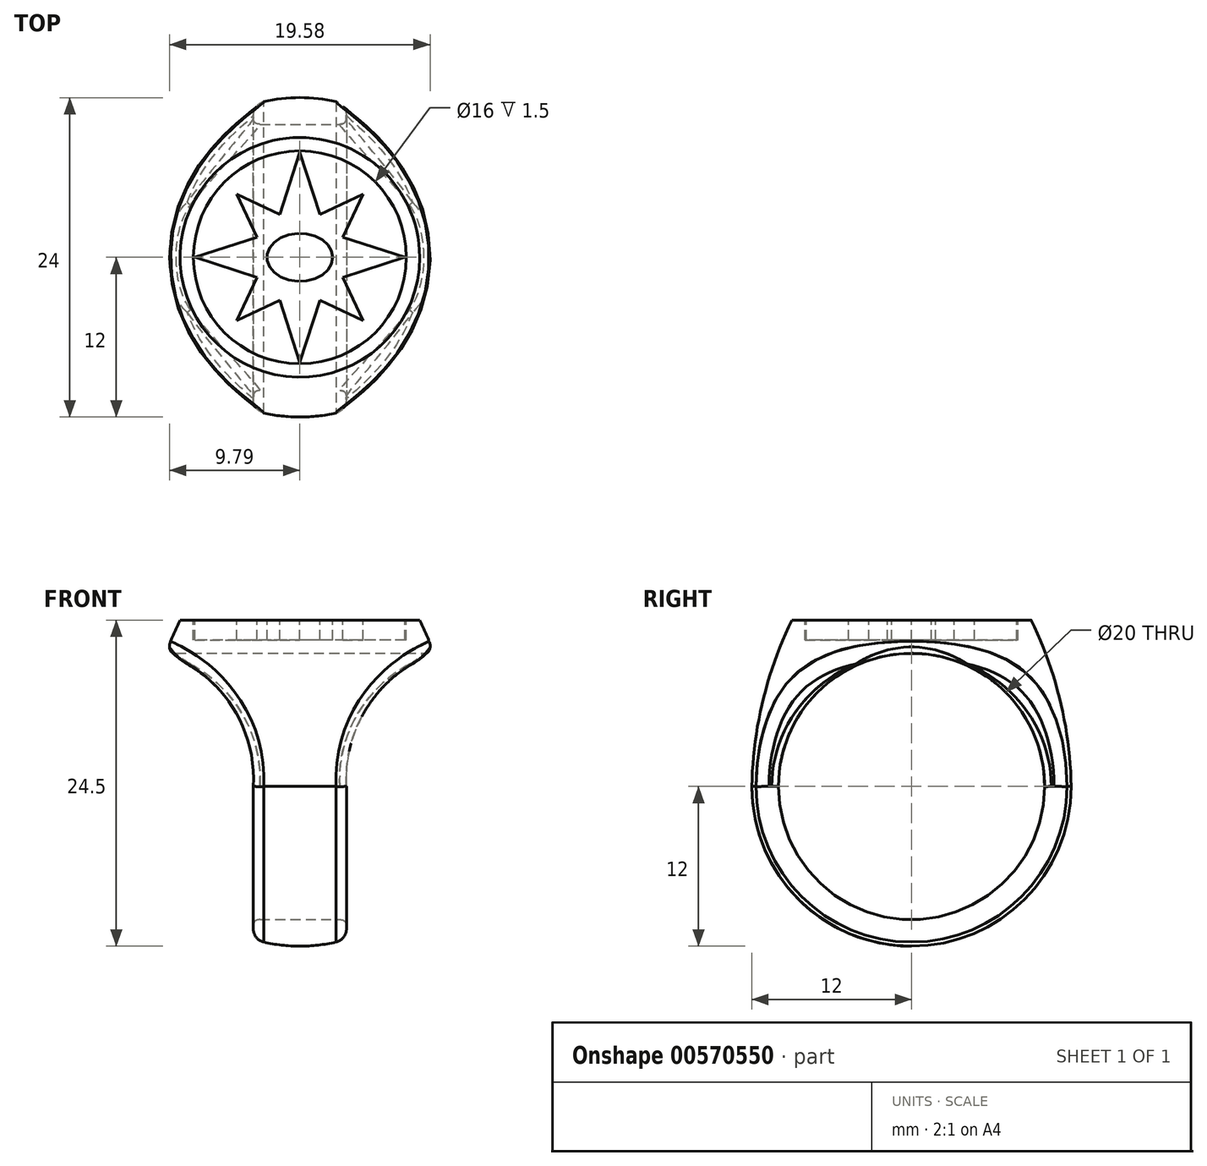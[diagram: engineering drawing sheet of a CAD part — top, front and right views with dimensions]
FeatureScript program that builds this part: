
annotation { "Feature Type Name" : "Feature", "Feature Type Description" : "" }
export const myFeature = defineFeature(function(context is Context, id is Id, definition is map)
    precondition{}
    {
        {
            var Q0;
            Q0=qCreatedBy(makeId("Right.planeOp"),FACE);
            var sketch = newSketch(context, id + "F0", { "sketchPlane" : qUnion([Q0])});
            skLineSegment(sketch, "E0", {"start": v(0, 0) * mm, "end": v(0, -24.5) * mm});
            skLineSegment(sketch, "E1", {"start": v(0, 0) * mm, "end": v(-9, 0) * mm});
            skArc(sketch, "E2", {"start": v(-12, -12.5) * mm, "mid": v(-8.49, -20.99) * mm, "end": v(0, -24.5) * mm});
            skLineSegment(sketch, "E3", {"start": v(0, -12.5) * mm, "end": v(-12, -12.5) * mm, "construction": true});
            skArc(sketch, "E4", {"start": v(-9, 0) * mm, "mid": v(-11.18, -6.09) * mm, "end": v(-12, -12.5) * mm});
            skSolve(sketch);
        }
        {
            var Q0;
            Q0=makeQuery(id+"F0.imprint","IMPRINT",FACE,{"disambiguationData":[TD([[makeQuery(id+"F0.imprint","IMPRINT",EDGE,{"derivedFrom":sQuery(id+"F0.wireOp",EDGE,"E0")}),-1.0]])]});
            var Q1;
            Q1=sQuery(id+"F0.wireOp",EDGE,"E0");
            revolve(context, id + "F1", {"entities" : qUnion([Q0]), "axis" : qUnion([Q1]), "revolveType" : RevolveType.FULL});
        }
        {
            var Q0;
            Q0=qCreatedBy(makeId("Right.planeOp"),FACE);
            var sketch = newSketch(context, id + "F2", { "sketchPlane" : qUnion([Q0])});
            skCircle(sketch, "E5", {"center": v(0, -12.5) * mm, "radius": 10 * mm});
            skSolve(sketch);
        }
        {
            var Q0;
            Q0=qSketchRegion(id+"F2",true);
            extrude(context, id + "F3", {"entities" : qUnion([Q0]), "operationType" : NewBodyOperationType.REMOVE, "oppositeDirection" : true, "depth" : 25 * mm, "offsetDistance" : 25 * mm, "symmetric" : true});
        }
        {
            var Q0;
            Q0=qCreatedBy(makeId("Front.planeOp"),FACE);
            var sketch = newSketch(context, id + "F4", { "sketchPlane" : qUnion([Q0])});
            skLineSegment(sketch, "E6", {"start": v(3.5, -26.5) * mm, "end": v(3.5, -12.5) * mm});
            skArc(sketch, "E7", {"start": v(10.15, -2.5) * mm, "mid": v(5.16, -6.39) * mm, "end": v(3.5, -12.5) * mm});
            skLineSegment(sketch, "E8", {"start": v(10.15, -2.5) * mm, "end": v(11.65, -2.5) * mm});
            skLineSegment(sketch, "E9", {"start": v(11.65, -2.5) * mm, "end": v(11.65, -26.5) * mm});
            skLineSegment(sketch, "E10", {"start": v(11.65, -26.5) * mm, "end": v(3.5, -26.5) * mm});
            skPoint(sketch, "E11.start.orphan", {"position": v(0, -24.5) * mm});
            skLineSegment(sketch, "E12", {"start": v(0, 0) * mm, "end": v(0, -24.5) * mm, "construction": true});
            skLineSegment(sketch, "E13.MirrorCS", {"start": v(-3.5, -26.5) * mm, "end": v(-3.5, -12.5) * mm});
            skArc(sketch, "E14.MirrorCS", {"start": v(-10.15, -2.5) * mm, "mid": v(-5.16, -6.39) * mm, "end": v(-3.5, -12.5) * mm});
            skLineSegment(sketch, "E15.MirrorCS", {"start": v(-11.65, -2.5) * mm, "end": v(-11.65, -26.5) * mm});
            skLineSegment(sketch, "E16.MirrorCS", {"start": v(-11.65, -26.5) * mm, "end": v(-3.5, -26.5) * mm});
            skLineSegment(sketch, "E17.MirrorCS", {"start": v(-10.15, -2.5) * mm, "end": v(-11.65, -2.5) * mm});
            skSolve(sketch);
        }
        {
            var Q0;
            Q0=qSketchRegion(id+"F4",true);
            extrude(context, id + "F5", {"entities" : qUnion([Q0]), "operationType" : NewBodyOperationType.REMOVE, "depth" : 25 * mm, "offsetDistance" : 25 * mm, "symmetric" : true});
        }
        {
            var Q0;
            Q0=makeQuery(id+"F1.opRevolve","SWEPT_FACE",FACE,{"disambiguationData":[OSD([sQuery(id+"F0.wireOp",EDGE,"E1")])]});
            var sketch = newSketch(context, id + "F6", { "sketchPlane" : qUnion([Q0])});
            skCircle(sketch, "E18", {"center": v(0, 0) * mm, "radius": 8 * mm});
            skLineSegment(sketch, "E19", {"start": v(-8, 0) * mm, "end": v(8, 0) * mm, "construction": true});
            skEllipse(sketch, "E20", {"center": v(0, 0) * mm, "majorRadius": 2.47 * mm, "minorRadius": 1.8 * mm, "majorAxis": v(1, 0)});
            skLineSegment(sketch, "E21", {"start": v(0, 8) * mm, "end": v(0, -8) * mm, "construction": true});
            skPoint(sketch, "E21.startSnap0", {"position": v(0, 1.8) * mm});
            skPoint(sketch, "E21.endSnap0", {"position": v(0, -1.8) * mm});
            skLineSegment(sketch, "E22", {"start": v(0, 0) * mm, "end": v(5.66, -5.66) * mm, "construction": true});
            skCircle(sketch, "E23", {"center": v(0, 0) * mm, "radius": 3.55 * mm, "construction": true});
            skLineSegment(sketch, "E24", {"start": v(7.9, 0) * mm, "end": v(3.22, -1.5) * mm});
            skLineSegment(sketch, "E25", {"start": v(3.22, -1.5) * mm, "end": v(4.74, -4.74) * mm});
            skLineSegment(sketch, "E26", {"start": v(4.74, -4.74) * mm, "end": v(1.5, -3.22) * mm});
            skLineSegment(sketch, "E27", {"start": v(1.5, -3.22) * mm, "end": v(0, -7.9) * mm});
            skLineSegment(sketch, "E28.MirrorCS", {"start": v(1.5, 3.22) * mm, "end": v(0, 7.9) * mm});
            skLineSegment(sketch, "E29.MirrorCS", {"start": v(4.74, 4.74) * mm, "end": v(1.5, 3.22) * mm});
            skLineSegment(sketch, "E30.MirrorCS", {"start": v(3.22, 1.5) * mm, "end": v(4.74, 4.74) * mm});
            skLineSegment(sketch, "E31.MirrorCS", {"start": v(7.9, 0) * mm, "end": v(3.22, 1.5) * mm});
            skLineSegment(sketch, "E32.MirrorCS", {"start": v(-1.5, 3.22) * mm, "end": v(0, 7.9) * mm});
            skLineSegment(sketch, "E33.MirrorCS", {"start": v(-4.74, 4.74) * mm, "end": v(-1.5, 3.22) * mm});
            skLineSegment(sketch, "E34.MirrorCS", {"start": v(-3.22, 1.5) * mm, "end": v(-4.74, 4.74) * mm});
            skLineSegment(sketch, "E35.MirrorCS", {"start": v(-7.9, 0) * mm, "end": v(-3.22, 1.5) * mm});
            skLineSegment(sketch, "E36.MirrorCS", {"start": v(-7.9, 0) * mm, "end": v(-3.22, -1.5) * mm});
            skLineSegment(sketch, "E37.MirrorCS", {"start": v(-4.74, -4.74) * mm, "end": v(-1.5, -3.22) * mm});
            skLineSegment(sketch, "E38.MirrorCS", {"start": v(-1.5, -3.22) * mm, "end": v(0, -7.9) * mm});
            skLineSegment(sketch, "E39.MirrorCS", {"start": v(-3.22, -1.5) * mm, "end": v(-4.74, -4.74) * mm});
            skSolve(sketch);
        }
        {
            var Q0;
            Q0=makeQuery(id+"F6.imprint","IMPRINT",FACE,{"disambiguationData":[TD([[makeQuery(id+"F6.imprint","IMPRINT",EDGE,{"derivedFrom":sQuery(id+"F6.wireOp",EDGE,"E18")}),1.0]])]});
            var Q1;
            Q1=makeQuery(id+"F6.imprint","IMPRINT",FACE,{"disambiguationData":[TD([[makeQuery(id+"F6.imprint","IMPRINT",EDGE,{"derivedFrom":sQuery(id+"F6.wireOp",EDGE,"E20")}),1.0]])]});
            extrude(context, id + "F7", {"entities" : qUnion([Q0, Q1]), "operationType" : NewBodyOperationType.REMOVE, "oppositeDirection" : true, "depth" : 1.5 * mm, "offsetDistance" : 25 * mm});
        }
        {
            var Q0;
            Q0=makeQuery(id+"F5.boolean.opBoolean","INTERSECT",EDGE,{"disambiguationData":[OD(1.0)],"derivedFrom":[makeQuery(id+"F1.opRevolve","SWEPT_FACE",FACE,{"disambiguationData":[OSD([sQuery(id+"F0.wireOp",EDGE,"E4")])]}),makeQuery(id+"F5.opExtrude","SWEPT_FACE",FACE,{"disambiguationData":[OSD([sQuery(id+"F4.wireOp",EDGE,"E14.MirrorCS")])]})]});
            var Q1;
            Q1=makeQuery(id+"F5.boolean.opBoolean","INTERSECT",EDGE,{"derivedFrom":[makeQuery(id+"F1.opRevolve","SWEPT_FACE",FACE,{"disambiguationData":[OSD([sQuery(id+"F0.wireOp",EDGE,"E2")])]}),makeQuery(id+"F5.opExtrude","SWEPT_FACE",FACE,{"disambiguationData":[OSD([sQuery(id+"F4.wireOp",EDGE,"E13.MirrorCS")])]})]});
            var Q2;
            Q2=makeQuery(id+"F5.boolean.opBoolean","INTERSECT",EDGE,{"disambiguationData":[OD(1.0)],"derivedFrom":[makeQuery(id+"F1.opRevolve","SWEPT_FACE",FACE,{"disambiguationData":[OSD([sQuery(id+"F0.wireOp",EDGE,"E4")])]}),makeQuery(id+"F5.opExtrude","SWEPT_FACE",FACE,{"disambiguationData":[OSD([sQuery(id+"F4.wireOp",EDGE,"E7")])]})]});
            var Q3;
            Q3=makeQuery(id+"F5.boolean.opBoolean","INTERSECT",EDGE,{"derivedFrom":[makeQuery(id+"F1.opRevolve","SWEPT_FACE",FACE,{"disambiguationData":[OSD([sQuery(id+"F0.wireOp",EDGE,"E2")])]}),makeQuery(id+"F5.opExtrude","SWEPT_FACE",FACE,{"disambiguationData":[OSD([sQuery(id+"F4.wireOp",EDGE,"E6")])]})]});
            fillet(context, id + "F8", {"entities" : qUnion([Q0, Q1, Q2, Q3]), "radius" : 1 * mm, "allowEdgeOverflow" : false});
        }
        {
            var Q0;
            Q0=makeQuery(id+"F5.boolean.opBoolean","INTERSECT",EDGE,{"disambiguationData":[OD(1.0)],"derivedFrom":[makeQuery(id+"F3.boolean.opBoolean","COPY",FACE,{"derivedFrom":makeQuery(id+"F3.opExtrude","SWEPT_FACE",FACE,{"disambiguationData":[OSD([sQuery(id+"F2.wireOp",EDGE,"E5")])]})}),makeQuery(id+"F5.opExtrude","SWEPT_FACE",FACE,{"disambiguationData":[OSD([sQuery(id+"F4.wireOp",EDGE,"E14.MirrorCS")])]})]});
            var Q1;
            Q1=makeQuery(id+"F5.boolean.opBoolean","INTERSECT",EDGE,{"derivedFrom":[makeQuery(id+"F3.boolean.opBoolean","COPY",FACE,{"derivedFrom":makeQuery(id+"F3.opExtrude","SWEPT_FACE",FACE,{"disambiguationData":[OSD([sQuery(id+"F2.wireOp",EDGE,"E5")])]})}),makeQuery(id+"F5.opExtrude","SWEPT_FACE",FACE,{"disambiguationData":[OSD([sQuery(id+"F4.wireOp",EDGE,"E13.MirrorCS")])]})]});
            var Q2;
            Q2=makeQuery(id+"F5.boolean.opBoolean","INTERSECT",EDGE,{"disambiguationData":[OD(0.0)],"derivedFrom":[makeQuery(id+"F3.boolean.opBoolean","COPY",FACE,{"derivedFrom":makeQuery(id+"F3.opExtrude","SWEPT_FACE",FACE,{"disambiguationData":[OSD([sQuery(id+"F2.wireOp",EDGE,"E5")])]})}),makeQuery(id+"F5.opExtrude","SWEPT_FACE",FACE,{"disambiguationData":[OSD([sQuery(id+"F4.wireOp",EDGE,"E14.MirrorCS")])]})]});
            var Q3;
            Q3=makeQuery(id+"F5.boolean.opBoolean","INTERSECT",EDGE,{"disambiguationData":[OD(0.0)],"derivedFrom":[makeQuery(id+"F3.boolean.opBoolean","COPY",FACE,{"derivedFrom":makeQuery(id+"F3.opExtrude","SWEPT_FACE",FACE,{"disambiguationData":[OSD([sQuery(id+"F2.wireOp",EDGE,"E5")])]})}),makeQuery(id+"F5.opExtrude","SWEPT_FACE",FACE,{"disambiguationData":[OSD([sQuery(id+"F4.wireOp",EDGE,"E7")])]})]});
            var Q4;
            Q4=makeQuery(id+"F3.boolean.opBoolean","COPY",FACE,{"derivedFrom":makeQuery(id+"F3.opExtrude","SWEPT_FACE",FACE,{"disambiguationData":[OSD([sQuery(id+"F2.wireOp",EDGE,"E5")])]})});
            fillet(context, id + "F9", {"entities" : qUnion([Q0, Q1, Q2, Q3, Q4]), "radius" : .5 * mm, "rho" : 0.5, "crossSection" : FilletCrossSection.CONIC, "allowEdgeOverflow" : false});
        }
    });
